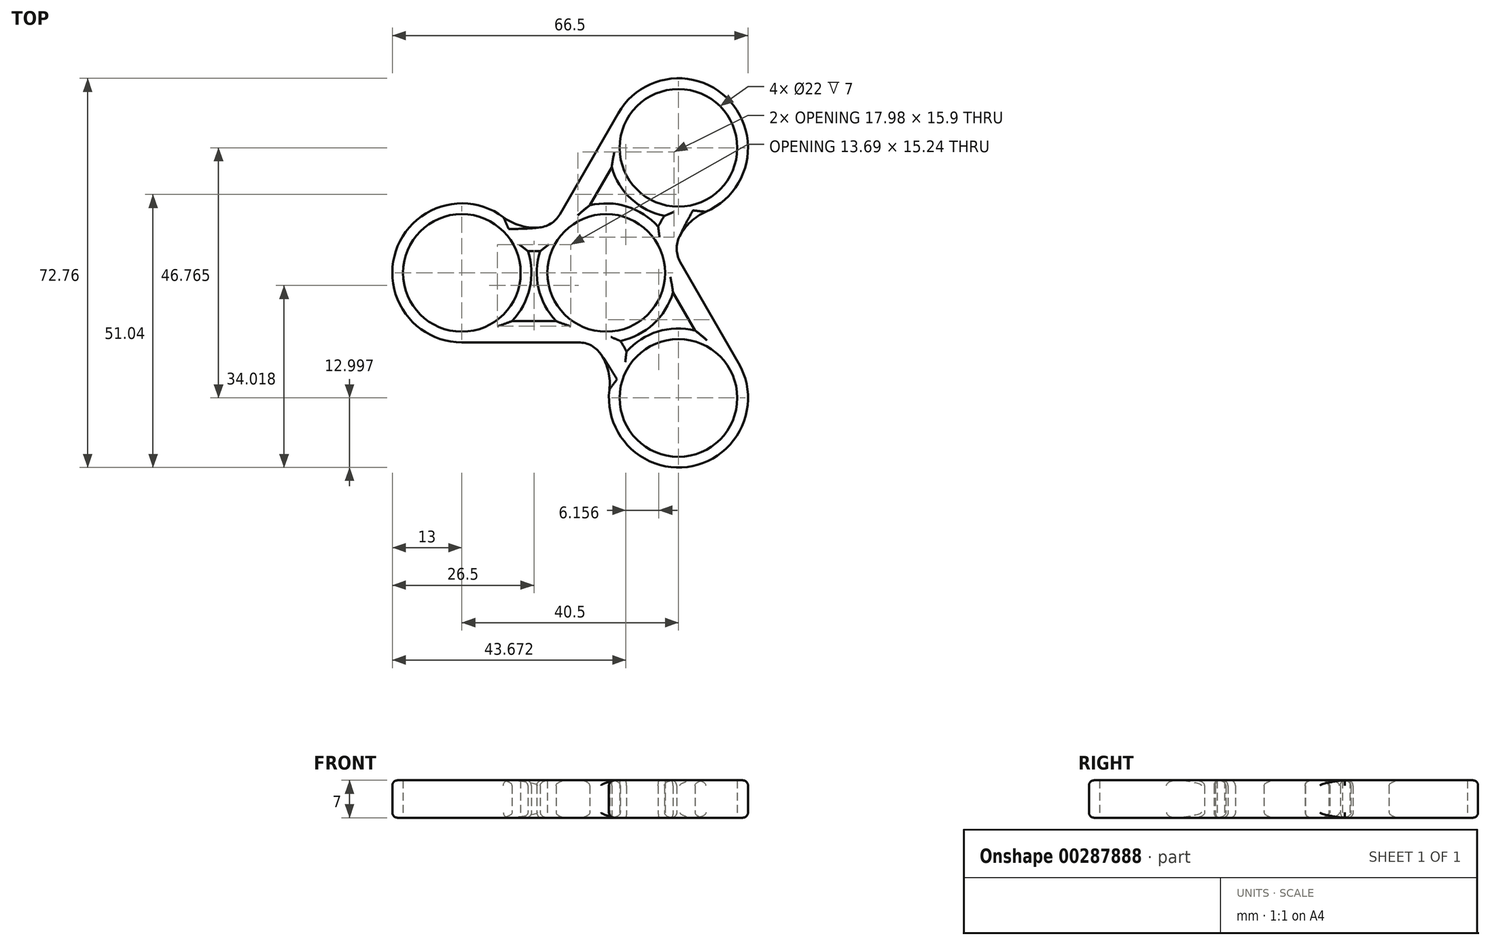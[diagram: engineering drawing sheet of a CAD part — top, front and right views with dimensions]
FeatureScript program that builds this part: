
annotation { "Feature Type Name" : "Feature", "Feature Type Description" : "" }
export const myFeature = defineFeature(function(context is Context, id is Id, definition is map)
    precondition{}
    {
        {
            var Q0;
            Q0=qCreatedBy(makeId("Top.planeOp"),FACE);
            var sketch = newSketch(context, id + "F0", { "sketchPlane" : qUnion([Q0])});
            skCircle(sketch, "E0", {"center": v(0, 0) * mm, "radius": 13 * mm});
            skCircle(sketch, "E1", {"center": v(-27, 0) * mm, "radius": 13 * mm});
            skLineSegment(sketch, "E2", {"start": v(-5.15, -13) * mm, "end": v(-27, -13) * mm});
            skCircle(sketch, "E3", {"center": v(-27, 0) * mm, "radius": 11 * mm});
            skCircle(sketch, "E4", {"center": v(0, 0) * mm, "radius": 11 * mm});
            skPoint(sketch, "E5", {"position": v(-17.69, 9.07) * mm});
            skPoint(sketch, "E6", {"position": v(-9.31, 9.07) * mm});
            skArc(sketch, "E7", {"start": v(-17.69, 9.07) * mm, "mid": v(-15.25, 8.56) * mm, "end": v(-12.75, 8.47) * mm});
            skLineSegment(sketch, "E8.1.0", {"start": v(13.84, 2.04) * mm, "end": v(24.76, -16.88) * mm});
            skCircle(sketch, "E8.1.1", {"center": v(13.5, -23.38) * mm, "radius": 13 * mm});
            skCircle(sketch, "E8.1.2", {"center": v(13.5, -23.38) * mm, "radius": 11 * mm});
            skArc(sketch, "E8.1.3", {"start": v(0.99, -19.85) * mm, "mid": v(0.21, -17.48) * mm, "end": v(-0.96, -15.28) * mm});
            skLineSegment(sketch, "E8.2.0", {"start": v(-8.68, 10.96) * mm, "end": v(2.24, 29.88) * mm});
            skCircle(sketch, "E8.2.1", {"center": v(13.5, 23.38) * mm, "radius": 13 * mm});
            skCircle(sketch, "E8.2.2", {"center": v(13.5, 23.38) * mm, "radius": 11 * mm});
            skArc(sketch, "E8.2.3", {"start": v(16.7, 10.78) * mm, "mid": v(15.03, 8.93) * mm, "end": v(13.71, 6.81) * mm});
            skPoint(sketch, "E9.orphan", {"position": v(0, -13) * mm});
            skPoint(sketch, "E10.orphan", {"position": v(11.26, 6.5) * mm});
            skPoint(sketch, "E11.orphan", {"position": v(-11.26, 6.5) * mm});
            skPoint(sketch, "E12.orphan", {"position": v(12.51, 3.53) * mm});
            skPoint(sketch, "E13.orphan", {"position": v(-3.2, -12.6) * mm});
            skPoint(sketch, "E14.visualSharp", {"position": v(-2.79, -13) * mm});
            skArc(sketch, "E14.filletArc", {"start": v(-0.96, -15.28) * mm, "mid": v(-2.77, -13.6) * mm, "end": v(-5.15, -13) * mm});
            skPoint(sketch, "E15.visualSharp", {"position": v(12.65, 4.09) * mm});
            skArc(sketch, "E15.filletArc", {"start": v(13.71, 6.81) * mm, "mid": v(13.17, 4.4) * mm, "end": v(13.84, 2.04) * mm});
            skPoint(sketch, "E16.visualSharp", {"position": v(-9.86, 8.91) * mm});
            skArc(sketch, "E16.filletArc", {"start": v(-12.75, 8.47) * mm, "mid": v(-10.4, 9.2) * mm, "end": v(-8.68, 10.96) * mm});
            skLineSegment(sketch, "E17.trimOffspring", {"start": v(-9.4, -8.98) * mm, "end": v(-17.6, -8.98) * mm});
            skArc(sketch, "E18.trimOffspring", {"start": v(-14.66, 4.08) * mm, "mid": v(-13.5, 4.05) * mm, "end": v(-12.34, 4.08) * mm});
            skArc(sketch, "E19.1.0", {"start": v(3.8, -14.74) * mm, "mid": v(3.24, -13.72) * mm, "end": v(2.63, -12.73) * mm});
            skLineSegment(sketch, "E19.1.1", {"start": v(12.48, -3.64) * mm, "end": v(16.58, -10.75) * mm});
            skArc(sketch, "E19.2.0", {"start": v(10.87, 10.65) * mm, "mid": v(10.26, 9.67) * mm, "end": v(9.7, 8.65) * mm});
            skLineSegment(sketch, "E19.2.1", {"start": v(-3.08, 12.63) * mm, "end": v(1.02, 19.74) * mm});
            skSolve(sketch);
        }
        {
            var Q0;
            Q0=makeQuery(id+"F0.imprint","IMPRINT",FACE,{"disambiguationData":[TD([[makeQuery(id+"F0.imprint","IMPRINT",EDGE,{"derivedFrom":sQuery(id+"F0.wireOp",EDGE,"E3")}),-1.0]])]});
            var Q1;
            Q1=makeQuery(id+"F0.imprint","IMPRINT",FACE,{"disambiguationData":[TD([[makeQuery(id+"F0.imprint","IMPRINT",EDGE,{"derivedFrom":sQuery(id+"F0.wireOp",EDGE,"E8.2.2")}),-1.0]])]});
            var Q2;
            Q2=makeQuery(id+"F0.imprint","IMPRINT",FACE,{"disambiguationData":[TD([[makeQuery(id+"F0.imprint","IMPRINT",EDGE,{"derivedFrom":sQuery(id+"F0.wireOp",EDGE,"E4")}),-1.0]])]});
            var Q3;
            Q3=makeQuery(id+"F0.imprint","IMPRINT",FACE,{"disambiguationData":[TD([[makeQuery(id+"F0.imprint","IMPRINT",EDGE,{"derivedFrom":sQuery(id+"F0.wireOp",EDGE,"E8.1.2")}),-1.0]])]});
            var Q4;
            {var subQ0=sQuery(id+"F0.wireOp",EDGE,"E7");Q4=makeQuery(id+"F0.imprint","IMPRINT",FACE,{"disambiguationData":[TD([[makeQuery(id+"F0.imprint","IMPRINT",EDGE,{"derivedFrom":subQ0}),-1.0]])]});}
            var Q5;
            {var subQ3=sQuery(id+"F0.wireOp",EDGE,"E2");Q5=makeQuery(id+"F0.imprint","IMPRINT",FACE,{"disambiguationData":[TD([[makeQuery(id+"F0.imprint","IMPRINT",EDGE,{"derivedFrom":subQ3}),-1.0]])]});}
            var Q6;
            {var subQ4=sQuery(id+"F0.wireOp",EDGE,"E8.1.0");Q6=makeQuery(id+"F0.imprint","IMPRINT",FACE,{"disambiguationData":[TD([[makeQuery(id+"F0.imprint","IMPRINT",EDGE,{"derivedFrom":subQ4}),-1.0]])]});}
            extrude(context, id + "F1", {"entities" : qUnion([Q0, Q1, Q2, Q3, Q4, Q5, Q6]), "depth" : 7 * mm});
        }
        {
            var Q0;
            Q0=makeQuery(id+"F1.opExtrude","CAP_EDGE",EDGE,{"disambiguationData":[OSD([sQuery(id+"F0.wireOp",EDGE,"E7")])],"isStart":true});
            var Q1;
            Q1=makeQuery(id+"F1.opExtrude","CAP_EDGE",EDGE,{"disambiguationData":[OSD([sQuery(id+"F0.wireOp",EDGE,"E16.filletArc")])],"isStart":true});
            var Q2;
            Q2=makeQuery(id+"F1.opExtrude","CAP_EDGE",EDGE,{"disambiguationData":[OSD([sQuery(id+"F0.wireOp",EDGE,"E8.2.0")])],"isStart":true});
            var Q3;
            Q3=makeQuery(id+"F1.opExtrude","CAP_EDGE",EDGE,{"disambiguationData":[OSD([sQuery(id+"F0.wireOp",EDGE,"E2")])],"isStart":true});
            var Q4;
            Q4=makeQuery(id+"F1.opExtrude","CAP_EDGE",EDGE,{"disambiguationData":[OSD([sQuery(id+"F0.wireOp",EDGE,"E8.1.3")])],"isStart":true});
            var Q5;
            Q5=makeQuery(id+"F1.opExtrude","CAP_EDGE",EDGE,{"disambiguationData":[OSD([sQuery(id+"F0.wireOp",EDGE,"E14.filletArc")])],"isStart":true});
            var Q6;
            Q6=makeQuery(id+"F1.opExtrude","CAP_EDGE",EDGE,{"disambiguationData":[OSD([sQuery(id+"F0.wireOp",EDGE,"E8.1.1")])],"isStart":true});
            var Q7;
            Q7=makeQuery(id+"F1.opExtrude","CAP_EDGE",EDGE,{"disambiguationData":[OSD([sQuery(id+"F0.wireOp",EDGE,"E8.1.0")])],"isStart":true});
            var Q8;
            Q8=makeQuery(id+"F1.opExtrude","CAP_EDGE",EDGE,{"disambiguationData":[OSD([sQuery(id+"F0.wireOp",EDGE,"E15.filletArc")])],"isStart":true});
            var Q9;
            Q9=makeQuery(id+"F1.opExtrude","CAP_EDGE",EDGE,{"disambiguationData":[OSD([sQuery(id+"F0.wireOp",EDGE,"E8.2.3")])],"isStart":true});
            var Q10;
            Q10=makeQuery(id+"F1.opExtrude","CAP_EDGE",EDGE,{"disambiguationData":[OSD([sQuery(id+"F0.wireOp",EDGE,"E8.2.1")])],"isStart":true});
            var Q11;
            Q11=makeQuery(id+"F1.opExtrude","CAP_EDGE",EDGE,{"disambiguationData":[OSD([sQuery(id+"F0.wireOp",EDGE,"E1")])],"isStart":true});
            var Q12;
            Q12=makeQuery(id+"F1.opExtrude","CAP_EDGE",EDGE,{"disambiguationData":[OSD([sQuery(id+"F0.wireOp",EDGE,"E7")])],"isStart":false});
            var Q13;
            Q13=makeQuery(id+"F1.opExtrude","CAP_EDGE",EDGE,{"disambiguationData":[OSD([sQuery(id+"F0.wireOp",EDGE,"E1")])],"isStart":false});
            var Q14;
            Q14=makeQuery(id+"F1.opExtrude","CAP_EDGE",EDGE,{"disambiguationData":[OSD([sQuery(id+"F0.wireOp",EDGE,"E8.2.0")])],"isStart":false});
            var Q15;
            Q15=makeQuery(id+"F1.opExtrude","CAP_EDGE",EDGE,{"disambiguationData":[OSD([sQuery(id+"F0.wireOp",EDGE,"E16.filletArc")])],"isStart":false});
            var Q16;
            Q16=makeQuery(id+"F1.opExtrude","CAP_EDGE",EDGE,{"disambiguationData":[OSD([sQuery(id+"F0.wireOp",EDGE,"E8.1.0")])],"isStart":false});
            var Q17;
            Q17=makeQuery(id+"F1.opExtrude","CAP_EDGE",EDGE,{"disambiguationData":[OSD([sQuery(id+"F0.wireOp",EDGE,"E2")])],"isStart":false});
            var Q18;
            Q18=makeQuery(id+"F1.opExtrude","CAP_EDGE",EDGE,{"disambiguationData":[OSD([sQuery(id+"F0.wireOp",EDGE,"E14.filletArc")])],"isStart":false});
            var Q19;
            Q19=makeQuery(id+"F1.opExtrude","CAP_EDGE",EDGE,{"disambiguationData":[OSD([sQuery(id+"F0.wireOp",EDGE,"E8.1.3")])],"isStart":false});
            var Q20;
            Q20=makeQuery(id+"F1.opExtrude","CAP_EDGE",EDGE,{"disambiguationData":[OSD([sQuery(id+"F0.wireOp",EDGE,"E8.1.1")])],"isStart":false});
            var Q21;
            Q21=makeQuery(id+"F1.opExtrude","CAP_EDGE",EDGE,{"disambiguationData":[OSD([sQuery(id+"F0.wireOp",EDGE,"E15.filletArc")])],"isStart":false});
            var Q22;
            Q22=makeQuery(id+"F1.opExtrude","CAP_EDGE",EDGE,{"disambiguationData":[OSD([sQuery(id+"F0.wireOp",EDGE,"E8.2.3")])],"isStart":false});
            var Q23;
            Q23=makeQuery(id+"F1.opExtrude","CAP_EDGE",EDGE,{"disambiguationData":[OSD([sQuery(id+"F0.wireOp",EDGE,"E8.2.1")])],"isStart":false});
            var Q24;
            {var subQ0=sQuery(id+"F0.wireOp",EDGE,"E0");Q24=makeQuery(id+"F1.opExtrude","CAP_EDGE",EDGE,{"disambiguationData":[OSD([subQ0]),TDD([makeQuery(id+"F0.imprint","IMPRINT",EDGE,{"disambiguationData":[TD([[makeQuery(id+"F0.imprint","INTERSECT",VERTEX,{"derivedFrom":[subQ0,sQuery(id+"F0.wireOp",EDGE,"E17.trimOffspring")]}),1.0]])],"derivedFrom":subQ0})])],"isStart":false});}
            var Q25;
            Q25=makeQuery(id+"F1.opExtrude","CAP_EDGE",EDGE,{"disambiguationData":[OSD([sQuery(id+"F0.wireOp",EDGE,"E18.trimOffspring")])],"isStart":false});
            var Q26;
            Q26=makeQuery(id+"F1.opExtrude","CAP_EDGE",EDGE,{"disambiguationData":[OSD([sQuery(id+"F0.wireOp",EDGE,"E17.trimOffspring")])],"isStart":false});
            var Q27;
            Q27=makeQuery(id+"F1.opExtrude","CAP_EDGE",EDGE,{"disambiguationData":[OSD([sQuery(id+"F0.wireOp",EDGE,"E19.1.0")])],"isStart":false});
            var Q28;
            {var subQ0=sQuery(id+"F0.wireOp",EDGE,"E0");Q28=makeQuery(id+"F1.opExtrude","CAP_EDGE",EDGE,{"disambiguationData":[OSD([subQ0]),TDD([makeQuery(id+"F0.imprint","IMPRINT",EDGE,{"disambiguationData":[TD([[makeQuery(id+"F0.imprint","INTERSECT",VERTEX,{"derivedFrom":[subQ0,sQuery(id+"F0.wireOp",EDGE,"E19.1.0")]}),-1.0]])],"derivedFrom":subQ0})])],"isStart":false});}
            var Q29;
            Q29=makeQuery(id+"F1.opExtrude","CAP_EDGE",EDGE,{"disambiguationData":[OSD([sQuery(id+"F0.wireOp",EDGE,"E19.1.1")])],"isStart":false});
            var Q30;
            Q30=makeQuery(id+"F1.opExtrude","CAP_EDGE",EDGE,{"disambiguationData":[OSD([sQuery(id+"F0.wireOp",EDGE,"E19.2.1")])],"isStart":false});
            var Q31;
            {var subQ0=sQuery(id+"F0.wireOp",EDGE,"E0");Q31=makeQuery(id+"F1.opExtrude","CAP_EDGE",EDGE,{"disambiguationData":[OSD([subQ0]),TDD([makeQuery(id+"F0.imprint","IMPRINT",EDGE,{"disambiguationData":[TD([[makeQuery(id+"F0.imprint","INTERSECT",VERTEX,{"derivedFrom":[subQ0,sQuery(id+"F0.wireOp",EDGE,"E19.2.0")]}),-1.0]])],"derivedFrom":subQ0})])],"isStart":false});}
            var Q32;
            Q32=makeQuery(id+"F1.opExtrude","CAP_EDGE",EDGE,{"disambiguationData":[OSD([sQuery(id+"F0.wireOp",EDGE,"E19.2.0")])],"isStart":false});
            var Q33;
            {var subQ0=sQuery(id+"F0.wireOp",EDGE,"E0");Q33=makeQuery(id+"F1.opExtrude","CAP_EDGE",EDGE,{"disambiguationData":[OSD([subQ0]),TDD([makeQuery(id+"F0.imprint","IMPRINT",EDGE,{"disambiguationData":[TD([[makeQuery(id+"F0.imprint","INTERSECT",VERTEX,{"derivedFrom":[subQ0,sQuery(id+"F0.wireOp",EDGE,"E19.2.0")]}),-1.0]])],"derivedFrom":subQ0})])],"isStart":true});}
            var Q34;
            Q34=makeQuery(id+"F1.opExtrude","CAP_EDGE",EDGE,{"disambiguationData":[OSD([sQuery(id+"F0.wireOp",EDGE,"E19.2.1")])],"isStart":true});
            var Q35;
            Q35=makeQuery(id+"F1.opExtrude","CAP_EDGE",EDGE,{"disambiguationData":[OSD([sQuery(id+"F0.wireOp",EDGE,"E19.2.0")])],"isStart":true});
            var Q36;
            Q36=makeQuery(id+"F1.opExtrude","CAP_EDGE",EDGE,{"disambiguationData":[OSD([sQuery(id+"F0.wireOp",EDGE,"E19.1.1")])],"isStart":true});
            var Q37;
            Q37=makeQuery(id+"F1.opExtrude","CAP_EDGE",EDGE,{"disambiguationData":[OSD([sQuery(id+"F0.wireOp",EDGE,"E19.1.0")])],"isStart":true});
            var Q38;
            {var subQ0=sQuery(id+"F0.wireOp",EDGE,"E0");Q38=makeQuery(id+"F1.opExtrude","CAP_EDGE",EDGE,{"disambiguationData":[OSD([subQ0]),TDD([makeQuery(id+"F0.imprint","IMPRINT",EDGE,{"disambiguationData":[TD([[makeQuery(id+"F0.imprint","INTERSECT",VERTEX,{"derivedFrom":[subQ0,sQuery(id+"F0.wireOp",EDGE,"E19.1.0")]}),-1.0]])],"derivedFrom":subQ0})])],"isStart":true});}
            var Q39;
            {var subQ0=sQuery(id+"F0.wireOp",EDGE,"E0");Q39=makeQuery(id+"F1.opExtrude","CAP_EDGE",EDGE,{"disambiguationData":[OSD([subQ0]),TDD([makeQuery(id+"F0.imprint","IMPRINT",EDGE,{"disambiguationData":[TD([[makeQuery(id+"F0.imprint","INTERSECT",VERTEX,{"derivedFrom":[subQ0,sQuery(id+"F0.wireOp",EDGE,"E17.trimOffspring")]}),1.0]])],"derivedFrom":subQ0})])],"isStart":true});}
            var Q40;
            Q40=makeQuery(id+"F1.opExtrude","CAP_EDGE",EDGE,{"disambiguationData":[OSD([sQuery(id+"F0.wireOp",EDGE,"E17.trimOffspring")])],"isStart":true});
            var Q41;
            Q41=makeQuery(id+"F1.opExtrude","CAP_EDGE",EDGE,{"disambiguationData":[OSD([sQuery(id+"F0.wireOp",EDGE,"E18.trimOffspring")])],"isStart":true});
            fillet(context, id + "F2", {"entities" : qUnion([Q0, Q1, Q2, Q3, Q4, Q5, Q6, Q7, Q8, Q9, Q10, Q11, Q12, Q13, Q14, Q15, Q16, Q17, Q18, Q19, Q20, Q21, Q22, Q23, Q24, Q25, Q26, Q27, Q28, Q29, Q30, Q31, Q32, Q33, Q34, Q35, Q36, Q37, Q38, Q39, Q40, Q41]), "radius" : 1 * mm, "tangentPropagation" : true, "allowEdgeOverflow" : false});
        }
        {
            var Q0;
            Q0=makeQuery(id+"F1.opExtrude","SWEPT_EDGE",EDGE,{"disambiguationData":[OSD([sQuery(id+"F0.wireOp",EDGE,"E1"),sQuery(id+"F0.wireOp",EDGE,"E7")])]});
            var Q1;
            Q1=makeQuery(id+"F1.opExtrude","SWEPT_EDGE",EDGE,{"disambiguationData":[OSD([sQuery(id+"F0.wireOp",EDGE,"E8.1.1"),sQuery(id+"F0.wireOp",EDGE,"E8.1.3")])]});
            var Q2;
            Q2=makeQuery(id+"F1.opExtrude","SWEPT_EDGE",EDGE,{"disambiguationData":[OSD([sQuery(id+"F0.wireOp",EDGE,"E8.2.1"),sQuery(id+"F0.wireOp",EDGE,"E8.2.3")])]});
            fillet(context, id + "F3", {"entities" : qUnion([Q0, Q1, Q2]), "radius" : 10 * mm, "tangentPropagation" : true, "allowEdgeOverflow" : false});
        }
    });
